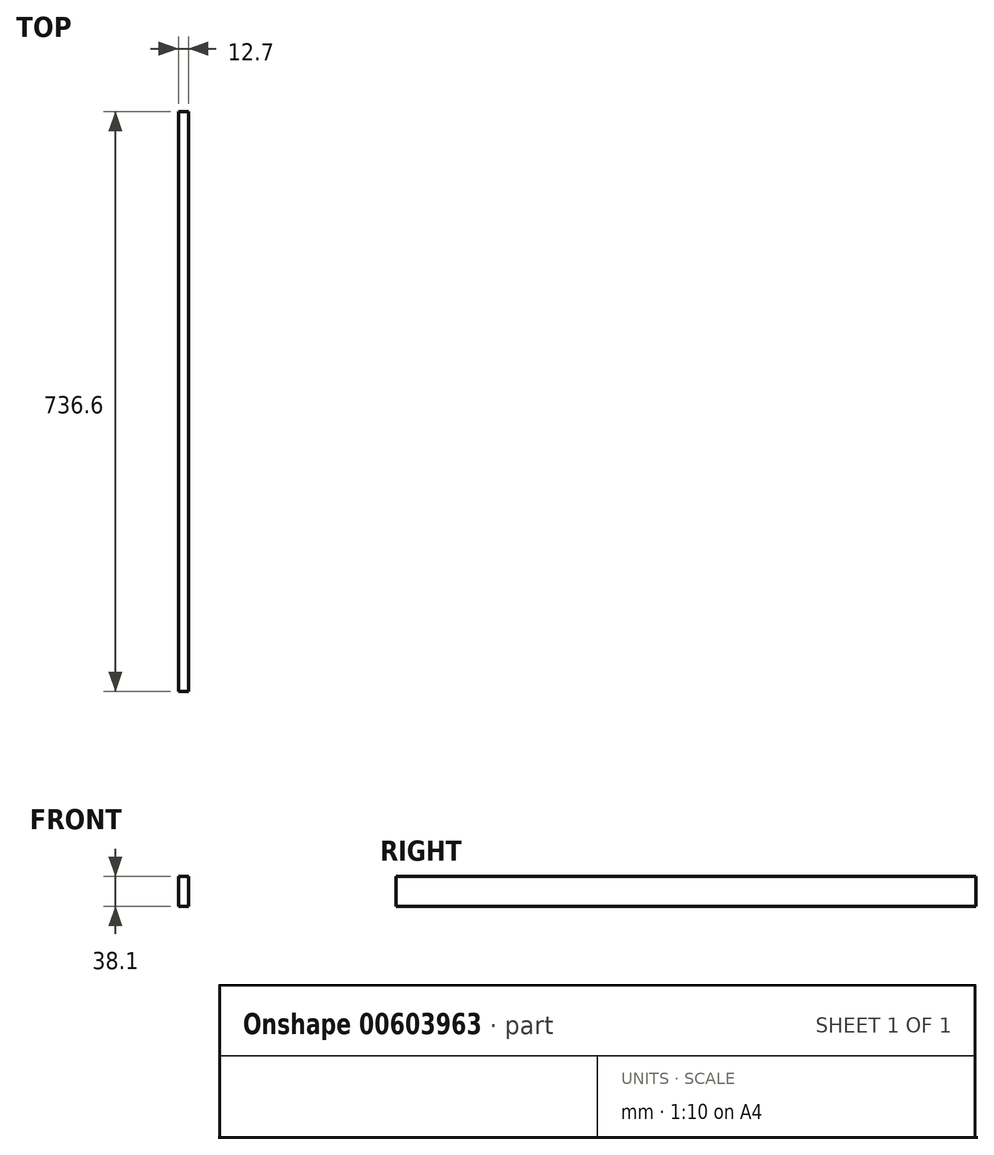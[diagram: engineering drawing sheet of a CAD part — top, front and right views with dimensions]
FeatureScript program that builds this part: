
annotation { "Feature Type Name" : "Feature", "Feature Type Description" : "" }
export const myFeature = defineFeature(function(context is Context, id is Id, definition is map)
    precondition{}
    {
        {
            var Q0;
            Q0=qCreatedBy(makeId("Right.planeOp"),FACE);
            var sketch = newSketch(context, id + "F0", { "sketchPlane" : qUnion([Q0])});
            skLineSegment(sketch, "E0.bottom", {"start": v(0, 0) * mm, "end": v(736.6, 0) * mm});
            skLineSegment(sketch, "E0.top", {"start": v(0, 38.1) * mm, "end": v(736.6, 38.1) * mm});
            skLineSegment(sketch, "E0.left", {"start": v(0, 0) * mm, "end": v(0, 38.1) * mm});
            skLineSegment(sketch, "E0.right", {"start": v(736.6, 0) * mm, "end": v(736.6, 38.1) * mm});
            skSolve(sketch);
        }
        {
            var Q0;
            Q0=makeQuery(id+"F0.imprint","IMPRINT",FACE,{"disambiguationData":[TD([[makeQuery(id+"F0.imprint","IMPRINT",EDGE,{"derivedFrom":sQuery(id+"F0.wireOp",EDGE,"E0.bottom")}),1.0]])]});
            extrude(context, id + "F1", {"entities" : qUnion([Q0]), "depth" : 12.7 * mm, "offsetDistance" : 25.4 * mm});
        }
    });
